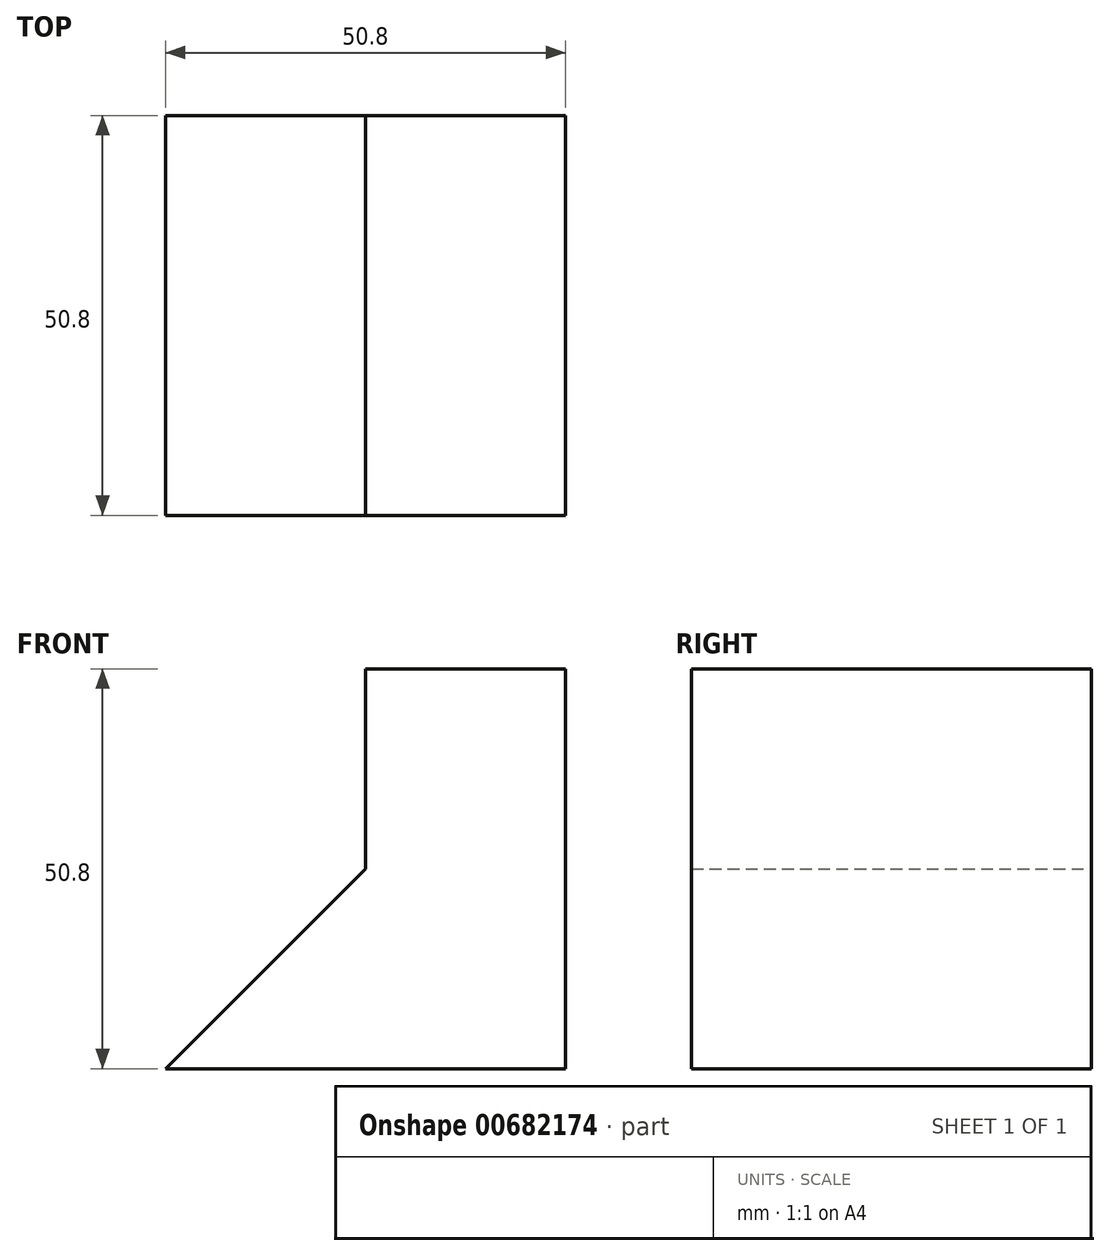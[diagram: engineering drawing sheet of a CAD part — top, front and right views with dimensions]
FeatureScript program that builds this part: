
annotation { "Feature Type Name" : "Feature", "Feature Type Description" : "" }
export const myFeature = defineFeature(function(context is Context, id is Id, definition is map)
    precondition{}
    {
        {
            var Q0;
            Q0=qCreatedBy(makeId("Front.planeOp"),FACE);
            var sketch = newSketch(context, id + "F0", { "sketchPlane" : qUnion([Q0])});
            skLineSegment(sketch, "E0", {"start": v(0, 0) * mm, "end": v(50.8, 0) * mm});
            skLineSegment(sketch, "E1", {"start": v(50.8, 0) * mm, "end": v(50.8, 50.8) * mm});
            skLineSegment(sketch, "E2", {"start": v(50.8, 50.8) * mm, "end": v(25.4, 50.8) * mm});
            skLineSegment(sketch, "E3", {"start": v(25.4, 50.8) * mm, "end": v(25.4, 25.4) * mm});
            skLineSegment(sketch, "E4", {"start": v(25.4, 25.4) * mm, "end": v(0, 0) * mm});
            skSolve(sketch);
        }
        {
            var Q0;
            Q0 = qSketchRegion(id + "F0", true);
            extrude(context, id + "F1", {"entities" : qUnion([Q0]), "depth" : 25.4 * mm, "offsetDistance" : 25.4 * mm});
        }
        {
            var Q0;
            Q0=makeQuery(id+"F1.opExtrude","CAP_FACE",FACE,{"disambiguationData":[OSD([sQuery(id+"F0.wireOp",EDGE,"E0"),sQuery(id+"F0.wireOp",EDGE,"E1"),sQuery(id+"F0.wireOp",EDGE,"E2"),sQuery(id+"F0.wireOp",EDGE,"E3"),sQuery(id+"F0.wireOp",EDGE,"E4")])],"isStart":false});
            extrude(context, id + "F2", {"entities" : qUnion([Q0]), "operationType" : NewBodyOperationType.ADD, "depth" : 25.4 * mm, "offsetDistance" : 25.4 * mm});
        }
    });
